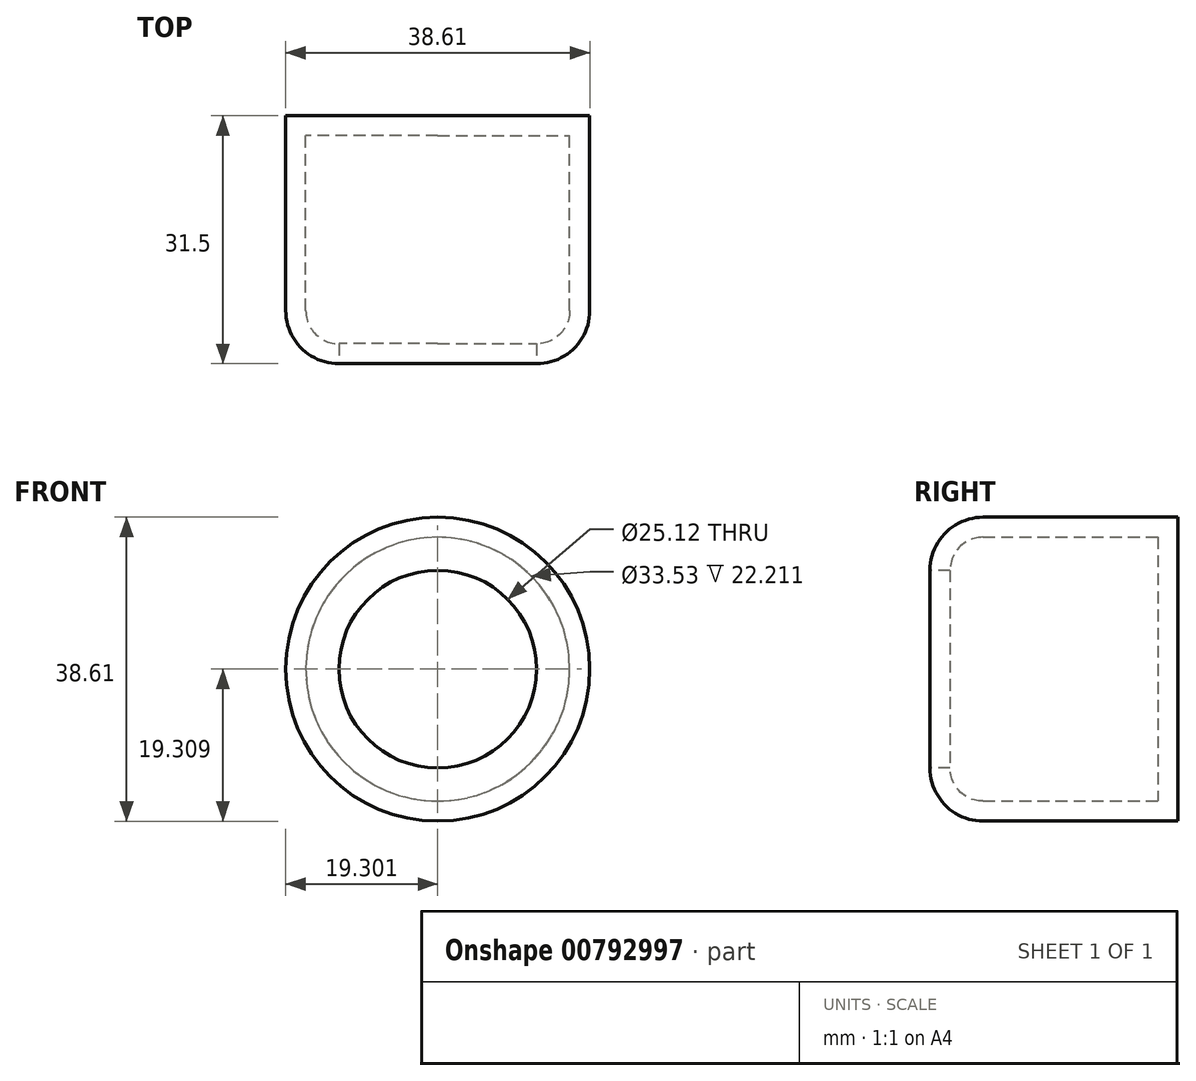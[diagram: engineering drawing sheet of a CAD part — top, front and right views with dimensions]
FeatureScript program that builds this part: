
annotation { "Feature Type Name" : "Feature", "Feature Type Description" : "" }
export const myFeature = defineFeature(function(context is Context, id is Id, definition is map)
    precondition{}
    {
        {
            var Q0;
            Q0=qCreatedBy(makeId("Front.planeOp"),FACE);
            var sketch = newSketch(context, id + "F0", { "sketchPlane" : qUnion([Q0])});
            skCircle(sketch, "E0", {"center": v(-28.44, 24.63) * mm, "radius": 19.3 * mm});
            skSolve(sketch);
        }
        {
            var Q0;
            Q0 = qSketchRegion(id + "F0", true);
            extrude(context, id + "F1", {"entities" : qUnion([Q0]), "depth" : 31.5 * mm, "offsetDistance" : 25.4 * mm});
        }
        {
            var Q0;
            Q0=makeQuery(id+"F1.opExtrude","CAP_EDGE",EDGE,{"disambiguationData":[OSD([sQuery(id+"F0.wireOp",EDGE,"E0")])],"isStart":false});
            fillet(context, id + "F2", {"entities" : qUnion([Q0]), "radius" : 6.75 * mm, "tangentPropagation" : true, "allowEdgeOverflow" : false});
        }
        {
            var Q0;
            Q0=makeQuery(id+"F1.opExtrude","CAP_FACE",FACE,{"disambiguationData":[OSD([sQuery(id+"F0.wireOp",EDGE,"E0")])],"isStart":false});
            shell(context, id + "F3", {"entities" : qUnion([Q0]), "thickness" : 2.54 * mm});
        }
    });
